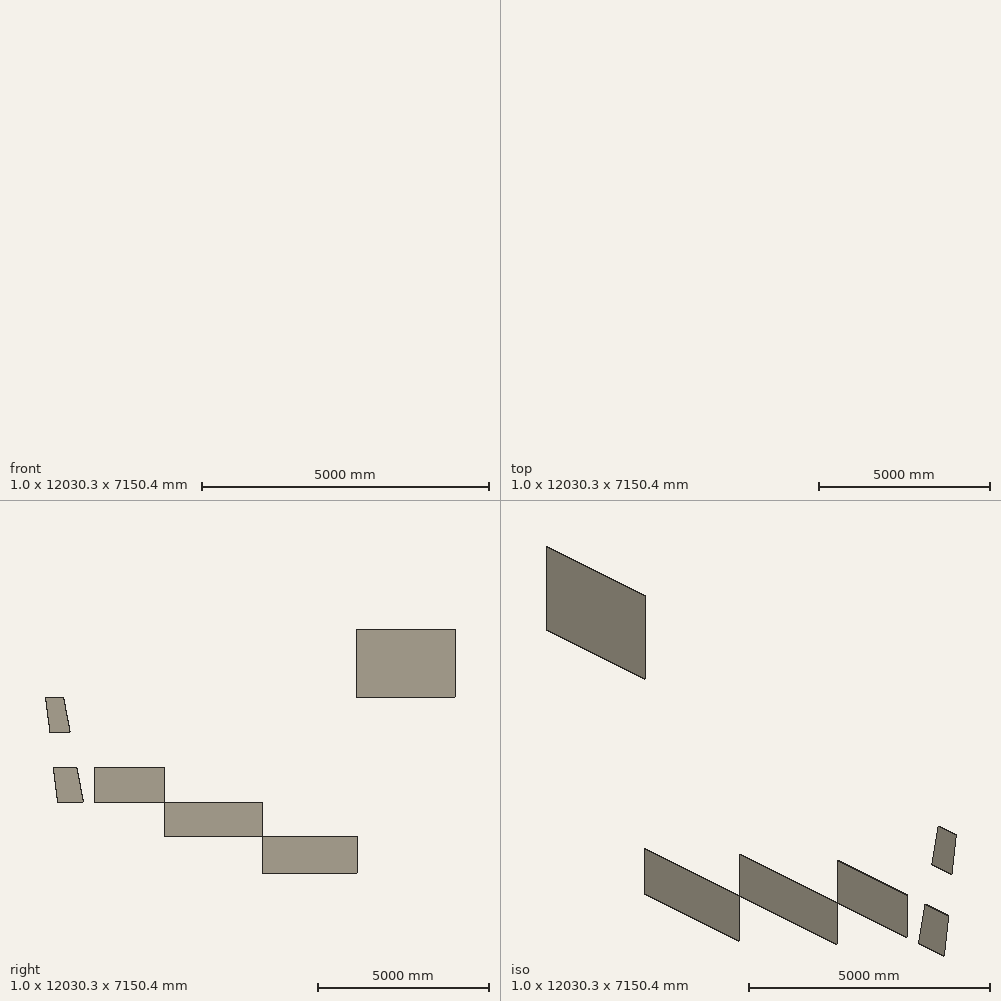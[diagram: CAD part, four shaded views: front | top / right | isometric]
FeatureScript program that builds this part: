
annotation { "Feature Type Name" : "Feature", "Feature Type Description" : "" }
export const myFeature = defineFeature(function(context is Context, id is Id, definition is map)
    precondition{}
    {
        {
            var Q0;
            Q0=qCreatedBy(makeId("Front.planeOp"),FACE);
            var sketch = newSketch(context, id + "F0", { "sketchPlane" : qUnion([Q0])});
            skLineSegment(sketch, "E0", {"start": v(0, 3570.74) * mm, "end": v(0, -6631.63) * mm, "construction": true});
            skLineSegment(sketch, "E1", {"start": v(-2995.9, 0) * mm, "end": v(5361.36, 0) * mm, "construction": true});
            skLineSegment(sketch, "E2", {"start": v(390.67, -17752.4) * mm, "end": v(6390.67, -17752.4) * mm, "construction": true});
            skSolve(sketch);
        }
        {
            var Q0;
            Q0=qCreatedBy(makeId("Right.planeOp"),FACE);
            var sketch = newSketch(context, id + "F1", { "sketchPlane" : qUnion([Q0])});
            skLineSegment(sketch, "E3", {"start": v(22652.95, 8444.73) * mm, "end": v(37652.95, 8444.73) * mm, "construction": true});
            skLineSegment(sketch, "E4", {"start": v(0, 0) * mm, "end": v(-26832.38, 0) * mm, "construction": true});
            skLineSegment(sketch, "E5", {"start": v(0, 0) * mm, "end": v(0, 9431.6) * mm, "construction": true});
            skSolve(sketch);
        }
        {
            var Q0;
            Q0=qCreatedBy(makeId("Right.planeOp"),FACE);
            var sketch = newSketch(context, id + "F2", { "sketchPlane" : qUnion([Q0])});
            skLineSegment(sketch, "E6", {"start": v(-19764.31, 1021.95) * mm, "end": v(-19570.86, 0) * mm});
            skLineSegment(sketch, "E7", {"start": v(-19570.86, 0) * mm, "end": v(-19064.54, 0) * mm});
            skLineSegment(sketch, "E8", {"start": v(-19064.54, 0) * mm, "end": v(-19064.54, 1022.48) * mm});
            skLineSegment(sketch, "E9", {"start": v(-19764.31, 1021.95) * mm, "end": v(-19064.54, 1022.48) * mm});
            skLineSegment(sketch, "E10.bottom", {"start": v(-19064.54, 0) * mm, "end": v(-17006.21, 0) * mm});
            skLineSegment(sketch, "E10.top", {"start": v(-19064.54, -1025.85) * mm, "end": v(-17006.21, -1025.85) * mm});
            skLineSegment(sketch, "E10.left", {"start": v(-19064.54, 0) * mm, "end": v(-19064.54, -1025.85) * mm});
            skLineSegment(sketch, "E10.right", {"start": v(-17006.21, 0) * mm, "end": v(-17006.21, -1025.85) * mm});
            skLineSegment(sketch, "E11.bottom", {"start": v(-17006.21, -1025.85) * mm, "end": v(-14128.25, -1025.85) * mm});
            skLineSegment(sketch, "E11.top", {"start": v(-17006.21, -2030.97) * mm, "end": v(-14128.25, -2030.97) * mm});
            skLineSegment(sketch, "E11.left", {"start": v(-17006.21, -1025.85) * mm, "end": v(-17006.21, -2030.97) * mm});
            skLineSegment(sketch, "E11.right", {"start": v(-14128.25, -1025.85) * mm, "end": v(-14128.25, -2030.97) * mm});
            skLineSegment(sketch, "E12.bottom", {"start": v(-14128.25, -2030.97) * mm, "end": v(-11341.72, -2030.97) * mm});
            skLineSegment(sketch, "E12.top", {"start": v(-14128.25, -3117.46) * mm, "end": v(-11341.72, -3117.46) * mm});
            skLineSegment(sketch, "E12.left", {"start": v(-14128.25, -2030.97) * mm, "end": v(-14128.25, -3117.46) * mm});
            skLineSegment(sketch, "E12.right", {"start": v(-11341.72, -2030.97) * mm, "end": v(-11341.72, -3117.46) * mm});
            skLineSegment(sketch, "E13", {"start": v(-19764.31, 1021.95) * mm, "end": v(-19956.28, 2036.1) * mm});
            skLineSegment(sketch, "E14", {"start": v(-19956.28, 2036.1) * mm, "end": v(-20489.4, 2036.1) * mm});
            skLineSegment(sketch, "E15", {"start": v(-20489.4, 2036.1) * mm, "end": v(-20358.18, 1021.95) * mm});
            skLineSegment(sketch, "E16", {"start": v(-20358.18, 1021.95) * mm, "end": v(-19764.31, 1021.95) * mm});
            skLineSegment(sketch, "E17.bottom", {"start": v(-11366.8, 2036.2) * mm, "end": v(-8459.1, 2036.2) * mm});
            skLineSegment(sketch, "E17.top", {"start": v(-11366.8, 4032.9) * mm, "end": v(-8459.1, 4032.9) * mm});
            skLineSegment(sketch, "E17.left", {"start": v(-11366.8, 2036.2) * mm, "end": v(-11366.8, 4032.9) * mm});
            skLineSegment(sketch, "E17.right", {"start": v(-8459.1, 2036.2) * mm, "end": v(-8459.1, 4032.9) * mm});
            skLineSegment(sketch, "E18", {"start": v(-20260.05, 3640.85) * mm, "end": v(-19764.31, 1021.95) * mm, "construction": true});
            skLineSegment(sketch, "E19", {"start": v(-19764.31, 1021.95) * mm, "end": v(-18881.44, -3642.12) * mm, "construction": true});
            skLineSegment(sketch, "E20", {"start": v(-17006.21, -1025.85) * mm, "end": v(-19064.54, -1025.85) * mm});
            skLineSegment(sketch, "E21", {"start": v(-19376.68, -1025.85) * mm, "end": v(-19570.86, 0) * mm});
            skLineSegment(sketch, "E22", {"start": v(-19570.86, 0) * mm, "end": v(-20265.76, 0) * mm});
            skLineSegment(sketch, "E23", {"start": v(-20265.76, 0) * mm, "end": v(-20134.67, -1025.85) * mm});
            skLineSegment(sketch, "E24", {"start": v(-20134.67, -1025.85) * mm, "end": v(-19376.68, -1025.85) * mm});
            skSolve(sketch);
        }
        {
            var Q0;
            Q0=makeQuery(id+"F2.imprint","IMPRINT",FACE,{"disambiguationData":[TD([[makeQuery(id+"F2.imprint","IMPRINT",EDGE,{"derivedFrom":sQuery(id+"F2.wireOp",EDGE,"E10.bottom")}),-1.0]])]});
            var Q1;
            Q1=makeQuery(id+"F2.imprint","IMPRINT",FACE,{"disambiguationData":[TD([[makeQuery(id+"F2.imprint","IMPRINT",EDGE,{"derivedFrom":sQuery(id+"F2.wireOp",EDGE,"E11.bottom")}),-1.0]])]});
            var Q2;
            Q2=makeQuery(id+"F2.imprint","IMPRINT",FACE,{"disambiguationData":[TD([[makeQuery(id+"F2.imprint","IMPRINT",EDGE,{"derivedFrom":sQuery(id+"F2.wireOp",EDGE,"E12.bottom")}),-1.0]])]});
            var Q3;
            Q3=makeQuery(id+"F2.imprint","IMPRINT",FACE,{"disambiguationData":[TD([[makeQuery(id+"F2.imprint","IMPRINT",EDGE,{"derivedFrom":sQuery(id+"F2.wireOp",EDGE,"E13")}),1.0]])]});
            var Q4;
            {var subQ1=sQuery(id+"F2.wireOp",EDGE,"E17.bottom");Q4=makeQuery(id+"F2.imprint","IMPRINT",FACE,{"disambiguationData":[TD([[makeQuery(id+"F2.imprint","IMPRINT",EDGE,{"derivedFrom":subQ1}),1.0]])]});}
            var Q5;
            Q5=makeQuery(id+"F2.imprint","IMPRINT",FACE,{"disambiguationData":[TD([[makeQuery(id+"F2.imprint","IMPRINT",EDGE,{"derivedFrom":sQuery(id+"F2.wireOp",EDGE,"E7")}),-1.0]])]});
            var Q6;
            Q6=makeQuery(id+"F2.imprint","IMPRINT",FACE,{"disambiguationData":[TD([[makeQuery(id+"F2.imprint","IMPRINT",EDGE,{"derivedFrom":sQuery(id+"F2.wireOp",EDGE,"E21")}),1.0]])]});
            extrude(context, id + "F3", {"entities" : qUnion([Q0, Q1, Q2, Q3, Q4, Q5, Q6]), "depth" : 1 * mm, "offsetDistance" : 25 * mm});
        }
    });
